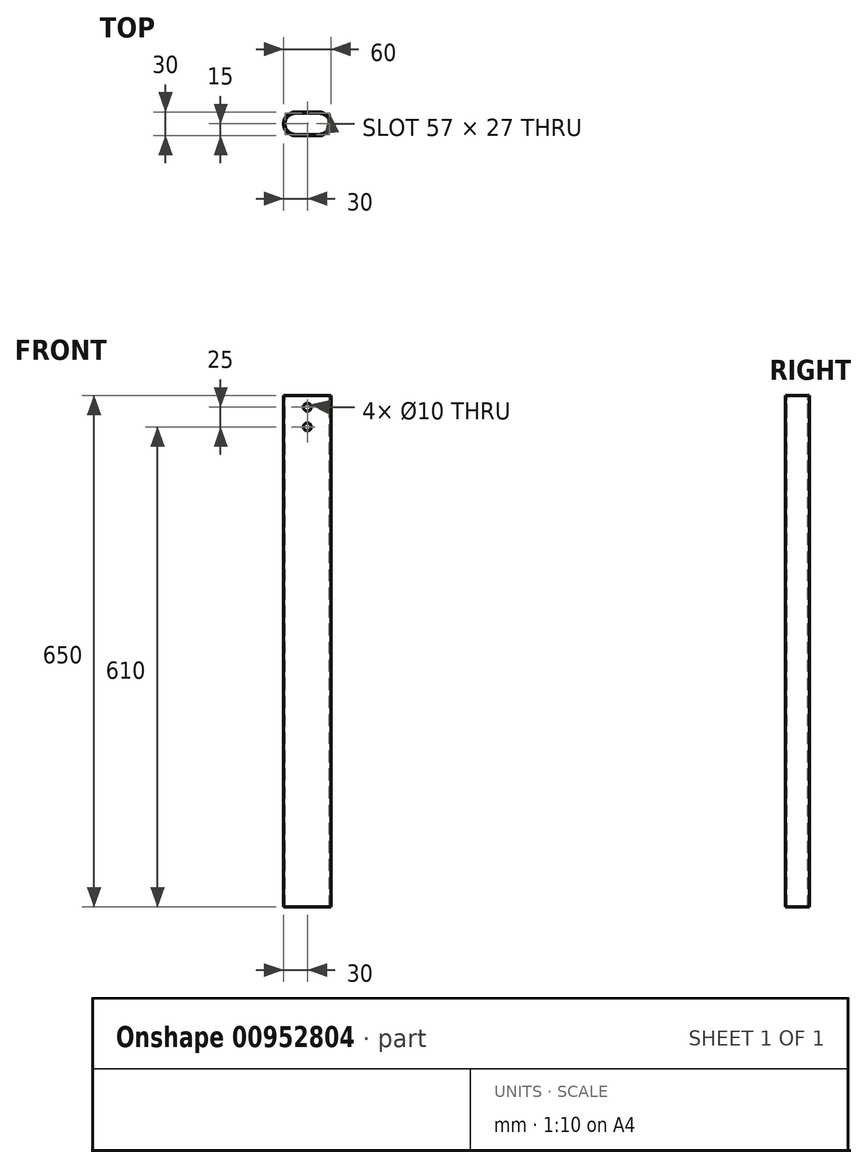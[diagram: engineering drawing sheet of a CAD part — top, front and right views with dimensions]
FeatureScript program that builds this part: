
annotation { "Feature Type Name" : "Feature", "Feature Type Description" : "" }
export const myFeature = defineFeature(function(context is Context, id is Id, definition is map)
    precondition{}
    {
        {
            var Q0;
            Q0=qCreatedBy(makeId("Top.planeOp"),FACE);
            var sketch = newSketch(context, id + "F0", { "sketchPlane" : qUnion([Q0])});
            skLineSegment(sketch, "E0.bottom", {"start": v(-15, 15) * mm, "end": v(15, 15) * mm});
            skLineSegment(sketch, "E0.top", {"start": v(-15, -15) * mm, "end": v(15, -15) * mm});
            skLineSegment(sketch, "E0.left", {"start": v(-30, 0) * mm, "end": v(-30, 0) * mm});
            skLineSegment(sketch, "E0.right", {"start": v(30, 0) * mm, "end": v(30, 0) * mm});
            skPoint(sketch, "E0.middle", {"position": v(0, 0) * mm});
            skPoint(sketch, "E1.visualSharp", {"position": v(-30, 15) * mm});
            skArc(sketch, "E1.filletArc", {"start": v(-15, 15) * mm, "mid": v(-25.6, 10.6) * mm, "end": v(-30, 0) * mm});
            skPoint(sketch, "E2.visualSharp", {"position": v(-30, -15) * mm});
            skArc(sketch, "E2.filletArc", {"start": v(-30, 0) * mm, "mid": v(-25.6, -10.6) * mm, "end": v(-15, -15) * mm});
            skPoint(sketch, "E3.visualSharp", {"position": v(30, -15) * mm});
            skArc(sketch, "E3.filletArc", {"start": v(15, -15) * mm, "mid": v(25.6, -10.6) * mm, "end": v(30, 0) * mm});
            skPoint(sketch, "E4.visualSharp", {"position": v(30, 15) * mm});
            skArc(sketch, "E4.filletArc", {"start": v(30, 0) * mm, "mid": v(25.6, 10.6) * mm, "end": v(15, 15) * mm});
            skLineSegment(sketch, "E5.bottom", {"start": v(-15, 13.5) * mm, "end": v(15, 13.5) * mm});
            skLineSegment(sketch, "E5.top", {"start": v(-15, -13.5) * mm, "end": v(15, -13.5) * mm});
            skLineSegment(sketch, "E5.left", {"start": v(-28.5, 0) * mm, "end": v(-28.5, 0) * mm});
            skLineSegment(sketch, "E5.right", {"start": v(28.5, 0) * mm, "end": v(28.5, 0) * mm});
            skPoint(sketch, "E6.visualSharp", {"position": v(-28.5, 13.5) * mm});
            skArc(sketch, "E6.filletArc", {"start": v(-15, 13.5) * mm, "mid": v(-24.55, 9.55) * mm, "end": v(-28.5, 0) * mm});
            skPoint(sketch, "E7.visualSharp", {"position": v(-28.5, -13.5) * mm});
            skArc(sketch, "E7.filletArc", {"start": v(-28.5, 0) * mm, "mid": v(-24.55, -9.55) * mm, "end": v(-15, -13.5) * mm});
            skPoint(sketch, "E8.visualSharp", {"position": v(28.5, -13.5) * mm});
            skArc(sketch, "E8.filletArc", {"start": v(15, -13.5) * mm, "mid": v(24.55, -9.55) * mm, "end": v(28.5, 0) * mm});
            skPoint(sketch, "E9.visualSharp", {"position": v(28.5, 13.5) * mm});
            skArc(sketch, "E9.filletArc", {"start": v(28.5, 0) * mm, "mid": v(24.55, 9.55) * mm, "end": v(15, 13.5) * mm});
            skSolve(sketch);
        }
        {
            var Q0;
            Q0 = qSketchRegion(id + "F0", true);
            extrude(context, id + "F1", {"entities" : qUnion([Q0]), "oppositeDirection" : true, "depth" : 650 * mm, "offsetDistance" : 25 * mm});
        }
        {
            var Q0;
            Q0=makeQuery(id+"F1.opExtrude","SWEPT_FACE",FACE,{"disambiguationData":[OSD([sQuery(id+"F0.wireOp",EDGE,"E0.bottom")])]});
            var sketch = newSketch(context, id + "F2", { "sketchPlane" : qUnion([Q0])});
            skLineSegment(sketch, "E10.0", {"start": v(15, 0) * mm, "end": v(-15, 0) * mm, "construction": true});
            skLineSegment(sketch, "E11", {"start": v(0, 0) * mm, "end": v(0, -15) * mm, "construction": true});
            skCircle(sketch, "E12", {"center": v(0, -15) * mm, "radius": 5 * mm});
            skLineSegment(sketch, "E13", {"start": v(0, -15) * mm, "end": v(0, -40) * mm, "construction": true});
            skCircle(sketch, "E14", {"center": v(0, -40) * mm, "radius": 5 * mm});
            skSolve(sketch);
        }
        {
            var Q0;
            Q0=makeQuery(id+"F2.imprint","IMPRINT",FACE,{"disambiguationData":[TD([[makeQuery(id+"F2.imprint","IMPRINT",EDGE,{"derivedFrom":sQuery(id+"F2.wireOp",EDGE,"E12")}),1.0]])]});
            var Q1;
            Q1=makeQuery(id+"F2.imprint","IMPRINT",FACE,{"disambiguationData":[TD([[makeQuery(id+"F2.imprint","IMPRINT",EDGE,{"derivedFrom":sQuery(id+"F2.wireOp",EDGE,"E14")}),1.0]])]});
            extrude(context, id + "F3", {"entities" : qUnion([Q0, Q1]), "operationType" : NewBodyOperationType.REMOVE, "oppositeDirection" : true, "depth" : 40 * mm, "offsetDistance" : 25 * mm});
        }
    });
